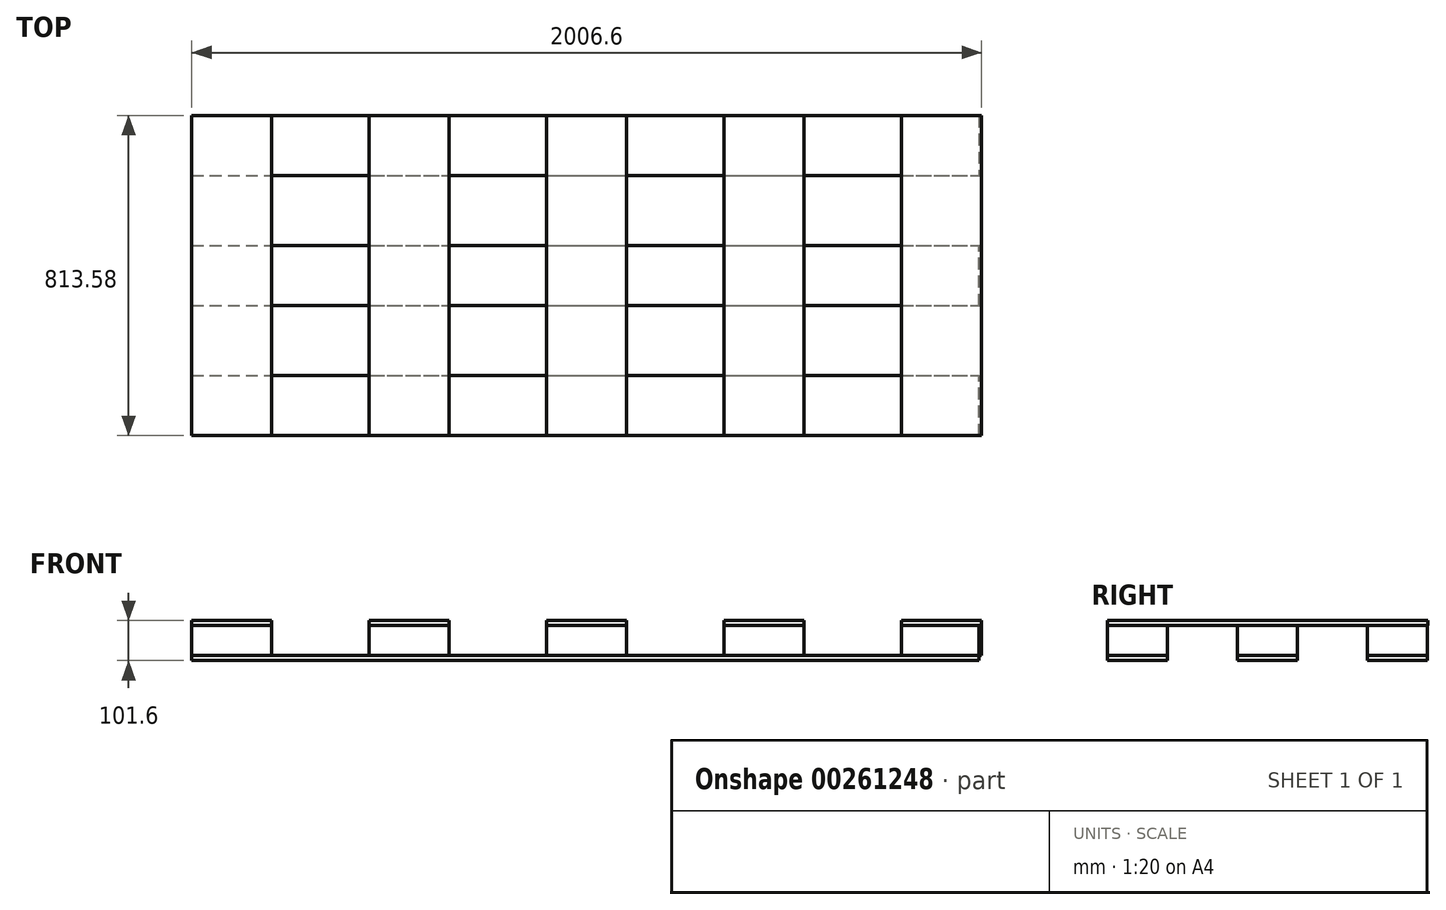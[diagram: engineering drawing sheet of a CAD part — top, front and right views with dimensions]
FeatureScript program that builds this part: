
annotation { "Feature Type Name" : "Feature", "Feature Type Description" : "" }
export const myFeature = defineFeature(function(context is Context, id is Id, definition is map)
    precondition{}
    {
        {
            var Q0;
            Q0=qCreatedBy(makeId("Top.planeOp"),FACE);
            var sketch = newSketch(context, id + "F0", { "sketchPlane" : qUnion([Q0])});
            skLineSegment(sketch, "E0.bottom", {"start": v(0, 0) * mm, "end": v(1999.74, 0) * mm});
            skLineSegment(sketch, "E0.top", {"start": v(0, 152.4) * mm, "end": v(1999.74, 152.4) * mm});
            skLineSegment(sketch, "E0.left", {"start": v(0, 0) * mm, "end": v(0, 152.4) * mm});
            skLineSegment(sketch, "E0.right", {"start": v(1999.74, 0) * mm, "end": v(1999.74, 152.4) * mm});
            skLineSegment(sketch, "E1.bottom", {"start": v(0, 330.2) * mm, "end": v(1999.74, 330.2) * mm});
            skLineSegment(sketch, "E1.top", {"start": v(0, 482.6) * mm, "end": v(1999.74, 482.6) * mm});
            skLineSegment(sketch, "E1.left", {"start": v(0, 330.2) * mm, "end": v(0, 482.6) * mm});
            skLineSegment(sketch, "E1.right", {"start": v(1999.74, 330.2) * mm, "end": v(1999.74, 482.6) * mm});
            skLineSegment(sketch, "E2.bottom", {"start": v(0, 812.8) * mm, "end": v(1999.74, 812.8) * mm});
            skLineSegment(sketch, "E2.top", {"start": v(0, 660.4) * mm, "end": v(1999.74, 660.4) * mm});
            skLineSegment(sketch, "E2.left", {"start": v(0, 812.8) * mm, "end": v(0, 660.4) * mm});
            skLineSegment(sketch, "E2.right", {"start": v(1999.74, 812.8) * mm, "end": v(1999.74, 660.4) * mm});
            skSolve(sketch);
        }
        {
            var Q0;
            Q0 = qSketchRegion(id + "F0", true);
            extrude(context, id + "F1", {"entities" : qUnion([Q0]), "depth" : 12.7 * mm});
        }
        {
            var Q0;
            Q0=makeQuery(id+"F1.opExtrude","CAP_FACE",FACE,{"disambiguationData":[OSD([sQuery(id+"F0.wireOp",EDGE,"E0.bottom"),sQuery(id+"F0.wireOp",EDGE,"E0.top"),sQuery(id+"F0.wireOp",EDGE,"E0.left"),sQuery(id+"F0.wireOp",EDGE,"E0.right")])],"isStart":false});
            var sketch = newSketch(context, id + "F2", { "sketchPlane" : qUnion([Q0])});
            skLineSegment(sketch, "E3.bottom", {"start": v(0, 0) * mm, "end": v(203.2, 0) * mm});
            skLineSegment(sketch, "E3.top", {"start": v(0, 152.4) * mm, "end": v(203.2, 152.4) * mm});
            skLineSegment(sketch, "E3.left", {"start": v(0, 0) * mm, "end": v(0, 152.4) * mm});
            skLineSegment(sketch, "E3.right", {"start": v(203.2, 0) * mm, "end": v(203.2, 152.4) * mm});
            skLineSegment(sketch, "E4.0.1.0", {"start": v(203.2, 330.2) * mm, "end": v(203.2, 482.6) * mm});
            skLineSegment(sketch, "E4.0.1.1", {"start": v(0, 330.2) * mm, "end": v(0, 482.6) * mm});
            skLineSegment(sketch, "E4.0.1.2", {"start": v(0, 482.6) * mm, "end": v(203.2, 482.6) * mm});
            skLineSegment(sketch, "E4.0.1.3", {"start": v(0, 330.2) * mm, "end": v(203.2, 330.2) * mm});
            skLineSegment(sketch, "E4.0.2.0", {"start": v(203.2, 660.4) * mm, "end": v(203.2, 812.8) * mm});
            skLineSegment(sketch, "E4.0.2.1", {"start": v(0, 660.4) * mm, "end": v(0, 812.8) * mm});
            skLineSegment(sketch, "E4.0.2.2", {"start": v(0, 812.8) * mm, "end": v(203.2, 812.8) * mm});
            skLineSegment(sketch, "E4.0.2.3", {"start": v(0, 660.4) * mm, "end": v(203.2, 660.4) * mm});
            skLineSegment(sketch, "E4.1.0.0", {"start": v(654.05, 0) * mm, "end": v(654.05, 152.4) * mm});
            skLineSegment(sketch, "E4.1.0.1", {"start": v(450.85, 0) * mm, "end": v(450.85, 152.4) * mm});
            skLineSegment(sketch, "E4.1.0.2", {"start": v(450.85, 152.4) * mm, "end": v(654.05, 152.4) * mm});
            skLineSegment(sketch, "E4.1.0.3", {"start": v(450.85, 0) * mm, "end": v(654.05, 0) * mm});
            skLineSegment(sketch, "E4.1.1.0", {"start": v(654.05, 330.2) * mm, "end": v(654.05, 482.6) * mm});
            skLineSegment(sketch, "E4.1.1.1", {"start": v(450.85, 330.2) * mm, "end": v(450.85, 482.6) * mm});
            skLineSegment(sketch, "E4.1.1.2", {"start": v(450.85, 482.6) * mm, "end": v(654.05, 482.6) * mm});
            skLineSegment(sketch, "E4.1.1.3", {"start": v(450.85, 330.2) * mm, "end": v(654.05, 330.2) * mm});
            skLineSegment(sketch, "E4.1.2.0", {"start": v(654.05, 660.4) * mm, "end": v(654.05, 812.8) * mm});
            skLineSegment(sketch, "E4.1.2.1", {"start": v(450.85, 660.4) * mm, "end": v(450.85, 812.8) * mm});
            skLineSegment(sketch, "E4.1.2.2", {"start": v(450.85, 812.8) * mm, "end": v(654.05, 812.8) * mm});
            skLineSegment(sketch, "E4.1.2.3", {"start": v(450.85, 660.4) * mm, "end": v(654.05, 660.4) * mm});
            skLineSegment(sketch, "E4.2.0.0", {"start": v(1104.9, 0) * mm, "end": v(1104.9, 152.4) * mm});
            skLineSegment(sketch, "E4.2.0.1", {"start": v(901.7, 0) * mm, "end": v(901.7, 152.4) * mm});
            skLineSegment(sketch, "E4.2.0.2", {"start": v(901.7, 152.4) * mm, "end": v(1104.9, 152.4) * mm});
            skLineSegment(sketch, "E4.2.0.3", {"start": v(901.7, 0) * mm, "end": v(1104.9, 0) * mm});
            skLineSegment(sketch, "E4.2.1.0", {"start": v(1104.9, 330.2) * mm, "end": v(1104.9, 482.6) * mm});
            skLineSegment(sketch, "E4.2.1.1", {"start": v(901.7, 330.2) * mm, "end": v(901.7, 482.6) * mm});
            skLineSegment(sketch, "E4.2.1.2", {"start": v(901.7, 482.6) * mm, "end": v(1104.9, 482.6) * mm});
            skLineSegment(sketch, "E4.2.1.3", {"start": v(901.7, 330.2) * mm, "end": v(1104.9, 330.2) * mm});
            skLineSegment(sketch, "E4.2.2.0", {"start": v(1104.9, 660.4) * mm, "end": v(1104.9, 812.8) * mm});
            skLineSegment(sketch, "E4.2.2.1", {"start": v(901.7, 660.4) * mm, "end": v(901.7, 812.8) * mm});
            skLineSegment(sketch, "E4.2.2.2", {"start": v(901.7, 812.8) * mm, "end": v(1104.9, 812.8) * mm});
            skLineSegment(sketch, "E4.2.2.3", {"start": v(901.7, 660.4) * mm, "end": v(1104.9, 660.4) * mm});
            skLineSegment(sketch, "E4.3.0.0", {"start": v(1555.75, 0) * mm, "end": v(1555.75, 152.4) * mm});
            skLineSegment(sketch, "E4.3.0.1", {"start": v(1352.55, 0) * mm, "end": v(1352.55, 152.4) * mm});
            skLineSegment(sketch, "E4.3.0.2", {"start": v(1352.55, 152.4) * mm, "end": v(1555.75, 152.4) * mm});
            skLineSegment(sketch, "E4.3.0.3", {"start": v(1352.55, 0) * mm, "end": v(1555.75, 0) * mm});
            skLineSegment(sketch, "E4.3.1.0", {"start": v(1555.75, 330.2) * mm, "end": v(1555.75, 482.6) * mm});
            skLineSegment(sketch, "E4.3.1.1", {"start": v(1352.55, 330.2) * mm, "end": v(1352.55, 482.6) * mm});
            skLineSegment(sketch, "E4.3.1.2", {"start": v(1352.55, 482.6) * mm, "end": v(1555.75, 482.6) * mm});
            skLineSegment(sketch, "E4.3.1.3", {"start": v(1352.55, 330.2) * mm, "end": v(1555.75, 330.2) * mm});
            skLineSegment(sketch, "E4.3.2.0", {"start": v(1555.75, 660.4) * mm, "end": v(1555.75, 812.8) * mm});
            skLineSegment(sketch, "E4.3.2.1", {"start": v(1352.55, 660.4) * mm, "end": v(1352.55, 812.8) * mm});
            skLineSegment(sketch, "E4.3.2.2", {"start": v(1352.55, 812.8) * mm, "end": v(1555.75, 812.8) * mm});
            skLineSegment(sketch, "E4.3.2.3", {"start": v(1352.55, 660.4) * mm, "end": v(1555.75, 660.4) * mm});
            skLineSegment(sketch, "E4.4.0.0", {"start": v(2006.6, 0) * mm, "end": v(2006.6, 152.4) * mm});
            skLineSegment(sketch, "E4.4.0.1", {"start": v(1803.4, 0) * mm, "end": v(1803.4, 152.4) * mm});
            skLineSegment(sketch, "E4.4.0.2", {"start": v(1803.4, 152.4) * mm, "end": v(2006.6, 152.4) * mm});
            skLineSegment(sketch, "E4.4.0.3", {"start": v(1803.4, 0) * mm, "end": v(2006.6, 0) * mm});
            skLineSegment(sketch, "E4.4.1.0", {"start": v(2006.6, 330.2) * mm, "end": v(2006.6, 482.6) * mm});
            skLineSegment(sketch, "E4.4.1.1", {"start": v(1803.4, 330.2) * mm, "end": v(1803.4, 482.6) * mm});
            skLineSegment(sketch, "E4.4.1.2", {"start": v(1803.4, 482.6) * mm, "end": v(2006.6, 482.6) * mm});
            skLineSegment(sketch, "E4.4.1.3", {"start": v(1803.4, 330.2) * mm, "end": v(2006.6, 330.2) * mm});
            skLineSegment(sketch, "E4.4.2.0", {"start": v(2006.6, 660.4) * mm, "end": v(2006.6, 812.8) * mm});
            skLineSegment(sketch, "E4.4.2.1", {"start": v(1803.4, 660.4) * mm, "end": v(1803.4, 812.8) * mm});
            skLineSegment(sketch, "E4.4.2.2", {"start": v(1803.4, 812.8) * mm, "end": v(2006.6, 812.8) * mm});
            skLineSegment(sketch, "E4.4.2.3", {"start": v(1803.4, 660.4) * mm, "end": v(2006.6, 660.4) * mm});
            skLineSegment(sketch, "E4.direction1", {"start": v(0, 0) * mm, "end": v(450.85, 0) * mm, "construction": true});
            skLineSegment(sketch, "E4.direction2", {"start": v(0, 0) * mm, "end": v(0, 330.2) * mm, "construction": true});
            skSolve(sketch);
        }
        {
            var Q0;
            Q0=makeQuery(id+"F2.imprint","IMPRINT",FACE,{"disambiguationData":[TD([[makeQuery(id+"F2.imprint","IMPRINT",EDGE,{"derivedFrom":sQuery(id+"F2.wireOp",EDGE,"E3.bottom")}),1.0]])]});
            var Q1;
            Q1=makeQuery(id+"F2.imprint","IMPRINT",FACE,{"disambiguationData":[TD([[makeQuery(id+"F2.imprint","IMPRINT",EDGE,{"derivedFrom":sQuery(id+"F2.wireOp",EDGE,"E4.1.0.0")}),1.0]])]});
            var Q2;
            Q2=makeQuery(id+"F2.imprint","IMPRINT",FACE,{"disambiguationData":[TD([[makeQuery(id+"F2.imprint","IMPRINT",EDGE,{"derivedFrom":sQuery(id+"F2.wireOp",EDGE,"E4.2.0.0")}),1.0]])]});
            var Q3;
            Q3=makeQuery(id+"F2.imprint","IMPRINT",FACE,{"disambiguationData":[TD([[makeQuery(id+"F2.imprint","IMPRINT",EDGE,{"derivedFrom":sQuery(id+"F2.wireOp",EDGE,"E4.3.0.0")}),1.0]])]});
            var Q4;
            {var subQ0=sQuery(id+"F2.wireOp",EDGE,"E4.4.0.1");Q4=makeQuery(id+"F2.imprint","IMPRINT",FACE,{"disambiguationData":[TD([[makeQuery(id+"F2.imprint","IMPRINT",EDGE,{"derivedFrom":subQ0}),-1.0]])]});}
            var Q5;
            Q5=makeQuery(id+"F2.imprint","IMPRINT",FACE,{"disambiguationData":[TD([[makeQuery(id+"F2.imprint","IMPRINT",EDGE,{"derivedFrom":sQuery(id+"F2.wireOp",EDGE,"E4.4.1.0")}),1.0]])]});
            var Q6;
            Q6=makeQuery(id+"F2.imprint","IMPRINT",FACE,{"disambiguationData":[TD([[makeQuery(id+"F2.imprint","IMPRINT",EDGE,{"derivedFrom":sQuery(id+"F2.wireOp",EDGE,"E4.3.1.0")}),1.0]])]});
            var Q7;
            Q7=makeQuery(id+"F2.imprint","IMPRINT",FACE,{"disambiguationData":[TD([[makeQuery(id+"F2.imprint","IMPRINT",EDGE,{"derivedFrom":sQuery(id+"F2.wireOp",EDGE,"E4.2.1.0")}),1.0]])]});
            var Q8;
            Q8=makeQuery(id+"F2.imprint","IMPRINT",FACE,{"disambiguationData":[TD([[makeQuery(id+"F2.imprint","IMPRINT",EDGE,{"derivedFrom":sQuery(id+"F2.wireOp",EDGE,"E4.1.1.0")}),1.0]])]});
            var Q9;
            Q9=makeQuery(id+"F2.imprint","IMPRINT",FACE,{"disambiguationData":[TD([[makeQuery(id+"F2.imprint","IMPRINT",EDGE,{"derivedFrom":sQuery(id+"F2.wireOp",EDGE,"E4.0.1.0")}),1.0]])]});
            var Q10;
            Q10=makeQuery(id+"F2.imprint","IMPRINT",FACE,{"disambiguationData":[TD([[makeQuery(id+"F2.imprint","IMPRINT",EDGE,{"derivedFrom":sQuery(id+"F2.wireOp",EDGE,"E4.0.2.0")}),1.0]])]});
            var Q11;
            Q11=makeQuery(id+"F2.imprint","IMPRINT",FACE,{"disambiguationData":[TD([[makeQuery(id+"F2.imprint","IMPRINT",EDGE,{"derivedFrom":sQuery(id+"F2.wireOp",EDGE,"E4.1.2.0")}),1.0]])]});
            var Q12;
            Q12=makeQuery(id+"F2.imprint","IMPRINT",FACE,{"disambiguationData":[TD([[makeQuery(id+"F2.imprint","IMPRINT",EDGE,{"derivedFrom":sQuery(id+"F2.wireOp",EDGE,"E4.2.2.0")}),1.0]])]});
            var Q13;
            Q13=makeQuery(id+"F2.imprint","IMPRINT",FACE,{"disambiguationData":[TD([[makeQuery(id+"F2.imprint","IMPRINT",EDGE,{"derivedFrom":sQuery(id+"F2.wireOp",EDGE,"E4.3.2.0")}),1.0]])]});
            var Q14;
            Q14=makeQuery(id+"F2.imprint","IMPRINT",FACE,{"disambiguationData":[TD([[makeQuery(id+"F2.imprint","IMPRINT",EDGE,{"derivedFrom":sQuery(id+"F2.wireOp",EDGE,"E4.4.2.0")}),1.0]])]});
            extrude(context, id + "F3", {"entities" : qUnion([Q0, Q1, Q2, Q3, Q4, Q5, Q6, Q7, Q8, Q9, Q10, Q11, Q12, Q13, Q14]), "depth" : 76.2 * mm});
        }
        {
            var Q0;
            Q0=makeQuery(id+"F3.opExtrude","CAP_FACE",FACE,{"disambiguationData":[OSD([sQuery(id+"F2.wireOp",EDGE,"E3.bottom"),sQuery(id+"F2.wireOp",EDGE,"E3.top"),sQuery(id+"F2.wireOp",EDGE,"E3.left"),sQuery(id+"F2.wireOp",EDGE,"E3.right")])],"isStart":false});
            var sketch = newSketch(context, id + "F4", { "sketchPlane" : qUnion([Q0])});
            skLineSegment(sketch, "E5.bottom", {"start": v(0, 0) * mm, "end": v(203.2, 0) * mm});
            skLineSegment(sketch, "E5.top", {"start": v(0, 813.58) * mm, "end": v(203.2, 813.58) * mm});
            skLineSegment(sketch, "E5.left", {"start": v(0, 0) * mm, "end": v(0, 813.58) * mm});
            skLineSegment(sketch, "E5.right", {"start": v(203.2, 0) * mm, "end": v(203.2, 813.58) * mm});
            skLineSegment(sketch, "E6.1.0.0", {"start": v(450.85, 813.58) * mm, "end": v(654.05, 813.58) * mm});
            skLineSegment(sketch, "E6.1.0.1", {"start": v(654.05, 0) * mm, "end": v(654.05, 813.58) * mm});
            skLineSegment(sketch, "E6.1.0.2", {"start": v(450.85, 0) * mm, "end": v(654.05, 0) * mm});
            skLineSegment(sketch, "E6.1.0.3", {"start": v(450.85, 0) * mm, "end": v(450.85, 813.58) * mm});
            skLineSegment(sketch, "E6.2.0.0", {"start": v(901.7, 813.58) * mm, "end": v(1104.9, 813.58) * mm});
            skLineSegment(sketch, "E6.2.0.1", {"start": v(1104.9, 0) * mm, "end": v(1104.9, 813.58) * mm});
            skLineSegment(sketch, "E6.2.0.2", {"start": v(901.7, 0) * mm, "end": v(1104.9, 0) * mm});
            skLineSegment(sketch, "E6.2.0.3", {"start": v(901.7, 0) * mm, "end": v(901.7, 813.58) * mm});
            skLineSegment(sketch, "E6.3.0.0", {"start": v(1352.55, 813.58) * mm, "end": v(1555.75, 813.58) * mm});
            skLineSegment(sketch, "E6.3.0.1", {"start": v(1555.75, 0) * mm, "end": v(1555.75, 813.58) * mm});
            skLineSegment(sketch, "E6.3.0.2", {"start": v(1352.55, 0) * mm, "end": v(1555.75, 0) * mm});
            skLineSegment(sketch, "E6.3.0.3", {"start": v(1352.55, 0) * mm, "end": v(1352.55, 813.58) * mm});
            skLineSegment(sketch, "E6.4.0.0", {"start": v(1803.4, 813.58) * mm, "end": v(2006.6, 813.58) * mm});
            skLineSegment(sketch, "E6.4.0.1", {"start": v(2006.6, 0) * mm, "end": v(2006.6, 813.58) * mm});
            skLineSegment(sketch, "E6.4.0.2", {"start": v(1803.4, 0) * mm, "end": v(2006.6, 0) * mm});
            skLineSegment(sketch, "E6.4.0.3", {"start": v(1803.4, 0) * mm, "end": v(1803.4, 813.58) * mm});
            skLineSegment(sketch, "E6.direction1", {"start": v(0, 0) * mm, "end": v(450.85, 0) * mm, "construction": true});
            skSolve(sketch);
        }
        {
            var Q0;
            {var subQ0=sQuery(id+"F4.wireOp",EDGE,"E5.bottom");Q0=makeQuery(id+"F4.imprint","IMPRINT",FACE,{"disambiguationData":[TD([[makeQuery(id+"F4.imprint","IMPRINT",EDGE,{"derivedFrom":subQ0}),1.0]])]});}
            var Q1;
            {var subQ0=sQuery(id+"F4.wireOp",EDGE,"E5.top");Q1=makeQuery(id+"F4.imprint","IMPRINT",FACE,{"disambiguationData":[TD([[makeQuery(id+"F4.imprint","IMPRINT",EDGE,{"derivedFrom":subQ0}),-1.0]])]});}
            var Q2;
            Q2=makeQuery(id+"F4.imprint","IMPRINT",FACE,{"disambiguationData":[TD([[makeQuery(id+"F4.imprint","IMPRINT",EDGE,{"derivedFrom":sQuery(id+"F4.wireOp",EDGE,"E6.1.0.0")}),-1.0]])]});
            var Q3;
            Q3=makeQuery(id+"F4.imprint","IMPRINT",FACE,{"disambiguationData":[TD([[makeQuery(id+"F4.imprint","IMPRINT",EDGE,{"derivedFrom":sQuery(id+"F4.wireOp",EDGE,"E6.2.0.0")}),-1.0]])]});
            var Q4;
            Q4=makeQuery(id+"F4.imprint","IMPRINT",FACE,{"disambiguationData":[TD([[makeQuery(id+"F4.imprint","IMPRINT",EDGE,{"derivedFrom":sQuery(id+"F4.wireOp",EDGE,"E6.3.0.0")}),-1.0]])]});
            var Q5;
            Q5=makeQuery(id+"F4.imprint","IMPRINT",FACE,{"disambiguationData":[TD([[makeQuery(id+"F4.imprint","IMPRINT",EDGE,{"derivedFrom":sQuery(id+"F4.wireOp",EDGE,"E6.4.0.0")}),-1.0]])]});
            extrude(context, id + "F5", {"entities" : qUnion([Q0, Q1, Q2, Q3, Q4, Q5]), "depth" : 12.7 * mm});
        }
    });
